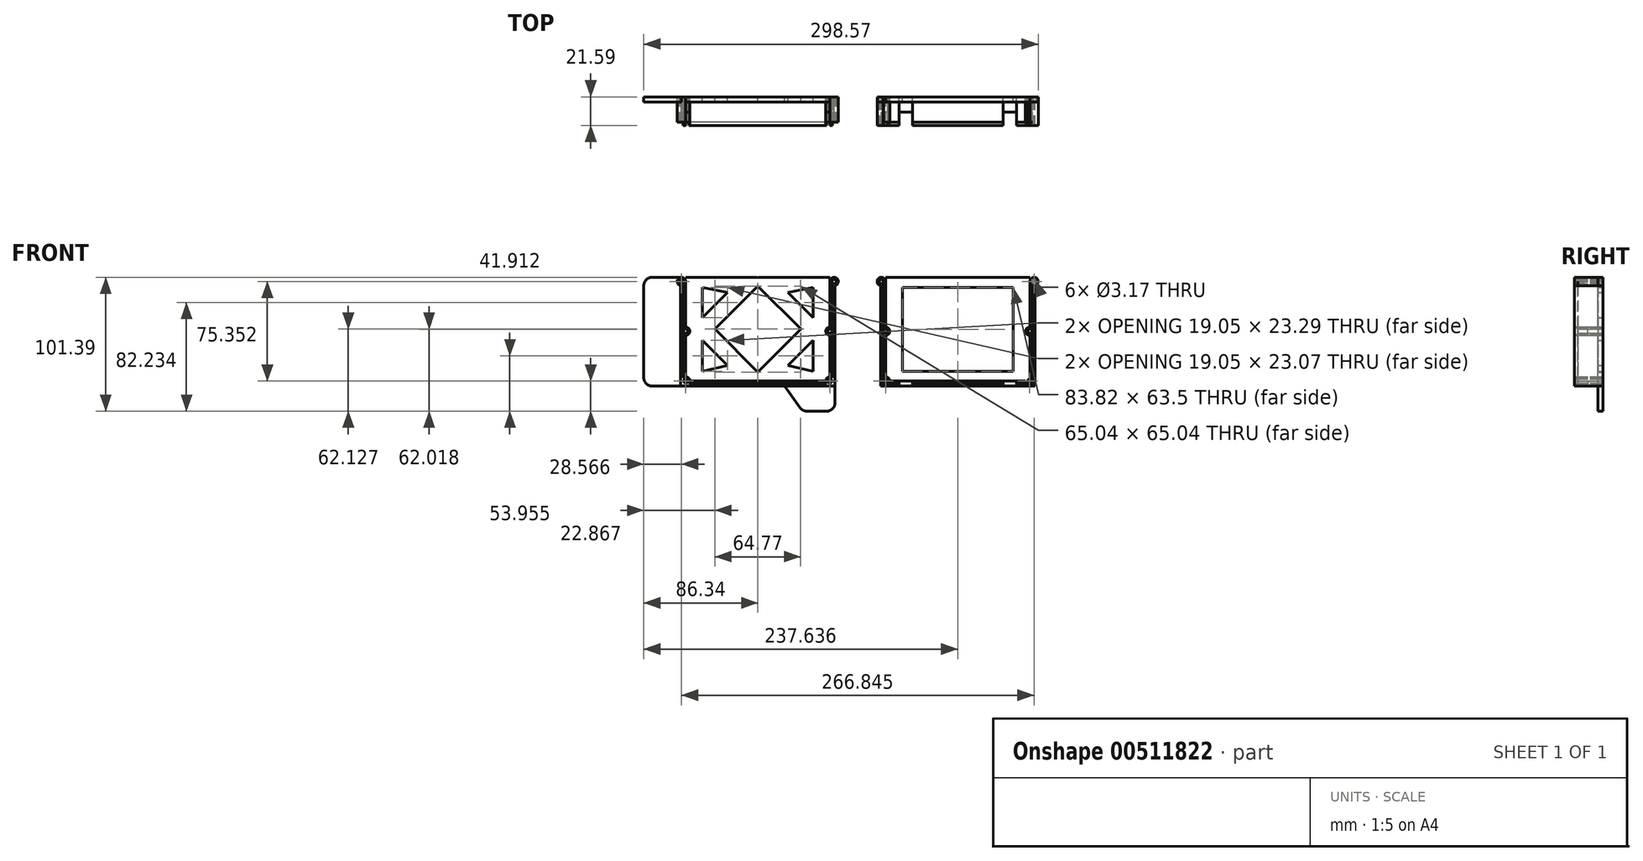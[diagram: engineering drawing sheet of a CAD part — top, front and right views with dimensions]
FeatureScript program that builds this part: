
annotation { "Feature Type Name" : "Feature", "Feature Type Description" : "" }
export const myFeature = defineFeature(function(context is Context, id is Id, definition is map)
    precondition{}
    {
        {
            var Q0;
            Q0=qCreatedBy(makeId("Front.planeOp"),FACE);
            var sketch = newSketch(context, id + "F0", { "sketchPlane" : qUnion([Q0])});
            skLineSegment(sketch, "E0.top", {"start": v(57.8, 40.84) * mm, "end": v(-57.77, 40.84) * mm});
            skPoint(sketch, "E0.middle", {"position": v(0, 0) * mm});
            skLineSegment(sketch, "E1.0", {"start": v(51.44, -37.67) * mm, "end": v(-51.34, -37.67) * mm});
            skLineSegment(sketch, "E2.0", {"start": v(-54.61, -34.5) * mm, "end": v(-54.61, -3.17) * mm});
            skLineSegment(sketch, "E3.0", {"start": v(54.6, -34.5) * mm, "end": v(54.6, -3.17) * mm});
            skLineSegment(sketch, "E4.0", {"start": v(-41.91, -30.27) * mm, "end": v(-41.91, -6.98) * mm});
            skLineSegment(sketch, "E5.0", {"start": v(41.91, -30.27) * mm, "end": v(41.91, -6.98) * mm});
            skLineSegment(sketch, "E6", {"start": v(-41.91, 10.16) * mm, "end": v(-22.86, 29.21) * mm});
            skLineSegment(sketch, "E7", {"start": v(-41.91, -6.98) * mm, "end": v(-22.86, -26.03) * mm});
            skLineSegment(sketch, "E8", {"start": v(22.86, -26.03) * mm, "end": v(41.9, -6.98) * mm});
            skLineSegment(sketch, "E9", {"start": v(41.9, 10.16) * mm, "end": v(22.86, 29.21) * mm});
            skLineSegment(sketch, "E10.trimOffspring", {"start": v(-41.91, 10.16) * mm, "end": v(-41.91, 33.23) * mm});
            skLineSegment(sketch, "E11.trimOffspring", {"start": v(41.91, 10.16) * mm, "end": v(41.91, 33.23) * mm});
            skLineSegment(sketch, "E12.trimOffspring", {"start": v(-22.86, 29.21) * mm, "end": v(-41.91, 33.23) * mm});
            skLineSegment(sketch, "E13.trimOffspring", {"start": v(-22.86, -26.03) * mm, "end": v(-41.91, -30.27) * mm});
            skLineSegment(sketch, "E14.trimOffspring", {"start": v(41.91, 33.23) * mm, "end": v(22.86, 29.21) * mm});
            skLineSegment(sketch, "E15.trimOffspring", {"start": v(41.91, -30.27) * mm, "end": v(22.86, -26.03) * mm});
            skLineSegment(sketch, "E16.0", {"start": v(-32.52, 1.59) * mm, "end": v(0, 34.1) * mm});
            skLineSegment(sketch, "E17.0", {"start": v(32.52, 1.59) * mm, "end": v(0, 34.1) * mm});
            skLineSegment(sketch, "E18.0", {"start": v(0, -30.93) * mm, "end": v(32.52, 1.59) * mm});
            skLineSegment(sketch, "E19.0", {"start": v(-32.52, 1.59) * mm, "end": v(0, -30.93) * mm});
            skArc(sketch, "E20", {"start": v(-54.61, -3.17) * mm, "mid": v(-51.44, 0) * mm, "end": v(-54.61, 3.18) * mm});
            skPoint(sketch, "E20.centerSnap0", {"position": v(-57.79, 0) * mm});
            skPoint(sketch, "E21.centerSnap0", {"position": v(57.79, 0) * mm});
            skArc(sketch, "E22", {"start": v(54.6, -34.5) * mm, "mid": v(52.36, -35.43) * mm, "end": v(51.44, -37.67) * mm});
            skPoint(sketch, "E23.second.point", {"position": v(54.6, 38.74) * mm});
            skPoint(sketch, "E23.third.point", {"position": v(60.92, 37.5) * mm});
            skLineSegment(sketch, "E24.trimOffspring", {"start": v(54.6, 3.18) * mm, "end": v(54.6, 40.84) * mm});
            skPoint(sketch, "E21.center.orphan", {"position": v(54.6, 0) * mm});
            skCircle(sketch, "E25", {"center": v(54.6, 0) * mm, "radius": 3.18 * mm});
            skCircle(sketch, "E26", {"center": v(54.6, 0) * mm, "radius": 1.6 * mm});
            skCircle(sketch, "E27", {"center": v(-54.61, 0) * mm, "radius": 3.18 * mm});
            skCircle(sketch, "E28", {"center": v(-54.61, 0) * mm, "radius": 1.6 * mm});
            skCircle(sketch, "E29", {"center": v(54.6, -37.67) * mm, "radius": 1.59 * mm});
            skCircle(sketch, "E30", {"center": v(54.6, -37.67) * mm, "radius": 3.18 * mm});
            skCircle(sketch, "E31", {"center": v(-54.51, -37.67) * mm, "radius": 3.17 * mm});
            skCircle(sketch, "E32", {"center": v(-54.51, -37.67) * mm, "radius": 1.59 * mm});
            skCircle(sketch, "E33", {"center": v(-57.77, 37.68) * mm, "radius": 3.16 * mm});
            skCircle(sketch, "E34", {"center": v(57.79, 37.67) * mm, "radius": 3.18 * mm});
            skCircle(sketch, "E35", {"center": v(-57.77, 37.68) * mm, "radius": 1.59 * mm});
            skCircle(sketch, "E36", {"center": v(57.79, 37.67) * mm, "radius": 1.6 * mm});
            skLineSegment(sketch, "E37", {"start": v(75.65, 45.82) * mm, "end": v(75.65, -59.82) * mm, "construction": true});
            skCircle(sketch, "E38.MirrorC", {"center": v(93.51, 37.67) * mm, "radius": 1.6 * mm});
            skCircle(sketch, "E39.MirrorC", {"center": v(209.07, 37.68) * mm, "radius": 1.59 * mm});
            skCircle(sketch, "E40.MirrorC", {"center": v(205.8, -37.67) * mm, "radius": 1.59 * mm});
            skCircle(sketch, "E41.MirrorC", {"center": v(96.69, 0) * mm, "radius": 1.6 * mm});
            skCircle(sketch, "E42.MirrorC", {"center": v(205.9, 0) * mm, "radius": 3.18 * mm});
            skCircle(sketch, "E43.MirrorC", {"center": v(96.69, -37.67) * mm, "radius": 1.59 * mm});
            skArc(sketch, "E44.MirrorCS", {"start": v(205.9, -3.17) * mm, "mid": v(202.73, 0) * mm, "end": v(205.9, 3.18) * mm});
            skCircle(sketch, "E45.MirrorC", {"center": v(96.69, 0) * mm, "radius": 3.18 * mm});
            skLineSegment(sketch, "E46.MirrorCS", {"start": v(99.86, -37.67) * mm, "end": v(202.63, -37.67) * mm});
            skCircle(sketch, "E47.MirrorC", {"center": v(205.9, 0) * mm, "radius": 1.6 * mm});
            skLineSegment(sketch, "E48.MirrorCS", {"start": v(205.9, -34.5) * mm, "end": v(205.9, -3.17) * mm});
            skLineSegment(sketch, "E49.MirrorCS", {"start": v(96.69, -34.5) * mm, "end": v(96.69, -3.17) * mm});
            skPoint(sketch, "E50.MirrorP", {"position": v(209.08, 0) * mm});
            skArc(sketch, "E51.MirrorCS", {"start": v(96.69, -34.5) * mm, "mid": v(98.93, -35.43) * mm, "end": v(99.86, -37.67) * mm});
            skCircle(sketch, "E52.MirrorC", {"center": v(209.07, 37.68) * mm, "radius": 3.16 * mm});
            skCircle(sketch, "E53.MirrorC", {"center": v(93.51, 37.67) * mm, "radius": 3.18 * mm});
            skLineSegment(sketch, "E54.MirrorCS", {"start": v(96.69, 3.18) * mm, "end": v(96.69, 40.84) * mm});
            skLineSegment(sketch, "E55.MirrorCS", {"start": v(93.5, 40.84) * mm, "end": v(209.07, 40.84) * mm});
            skPoint(sketch, "E56.MirrorP", {"position": v(90.38, 37.5) * mm});
            skLineSegment(sketch, "E57.MirrorCS", {"start": v(90.38, 37.5) * mm, "end": v(90.38, 37.16) * mm});
            skCircle(sketch, "E58.MirrorC", {"center": v(205.8, -37.67) * mm, "radius": 3.17 * mm});
            skCircle(sketch, "E59.MirrorC", {"center": v(96.69, -37.67) * mm, "radius": 3.18 * mm});
            skPoint(sketch, "E60.MirrorP", {"position": v(151.3, 0) * mm});
            skPoint(sketch, "E61.MirrorP", {"position": v(93.51, 0) * mm});
            skPoint(sketch, "E62.MirrorP", {"position": v(96.69, 38.74) * mm});
            skLineSegment(sketch, "E63.MirrorCS", {"start": v(205.9, 3.18) * mm, "end": v(205.9, 40.85) * mm});
            skLineSegment(sketch, "E64", {"start": v(109.39, 33.23) * mm, "end": v(193.2, 33.23) * mm});
            skLineSegment(sketch, "E65", {"start": v(109.39, 33.23) * mm, "end": v(109.39, -30.27) * mm});
            skLineSegment(sketch, "E66", {"start": v(109.39, -30.27) * mm, "end": v(193.2, -30.27) * mm});
            skLineSegment(sketch, "E67", {"start": v(193.2, 33.23) * mm, "end": v(193.2, -30.27) * mm});
            skLineSegment(sketch, "E68.0", {"start": v(185.59, -41.48) * mm, "end": v(185.59, -37.67) * mm});
            skLineSegment(sketch, "E69", {"start": v(195.75, -37.67) * mm, "end": v(195.75, -41.48) * mm});
            skLineSegment(sketch, "E70", {"start": v(117, -37.67) * mm, "end": v(117, -41.48) * mm});
            skLineSegment(sketch, "E71", {"start": v(106.85, -37.67) * mm, "end": v(106.85, -41.48) * mm});
            skLineSegment(sketch, "E72", {"start": v(-57.77, 40.84) * mm, "end": v(-79.99, 40.84) * mm});
            skPoint(sketch, "E73.visualSharp", {"position": v(-86.34, 40.84) * mm});
            skArc(sketch, "E73.filletArc", {"start": v(-79.99, 40.84) * mm, "mid": v(-84.48, 38.98) * mm, "end": v(-86.34, 34.5) * mm});
            skLineSegment(sketch, "E74.0", {"start": v(-58.4, 34.58) * mm, "end": v(-58.4, -41.49) * mm});
            skLineSegment(sketch, "E75.1", {"start": v(58.43, -41.49) * mm, "end": v(-58.4, -41.49) * mm});
            skLineSegment(sketch, "E76.0", {"start": v(52.07, -39.58) * mm, "end": v(-51.97, -39.58) * mm});
            skLineSegment(sketch, "E77", {"start": v(58.42, -44.02) * mm, "end": v(58.42, -54.19) * mm});
            skLineSegment(sketch, "E78.trimOffspring", {"start": v(56.51, -2.54) * mm, "end": v(56.51, -35.13) * mm});
            skLineSegment(sketch, "E79.trimOffspring", {"start": v(58.38, 34.55) * mm, "end": v(58.42, -44.02) * mm});
            skLineSegment(sketch, "E80.trimOffspring", {"start": v(56.52, 34.76) * mm, "end": v(56.52, 2.54) * mm});
            skLineSegment(sketch, "E81.trimOffspring", {"start": v(-56.52, 34.78) * mm, "end": v(-56.51, 2.54) * mm});
            skLineSegment(sketch, "E82.trimOffspring", {"start": v(-56.51, -2.54) * mm, "end": v(-56.51, -35.21) * mm});
            skLineSegment(sketch, "E83", {"start": v(37.17, -60.54) * mm, "end": v(52.07, -60.54) * mm});
            skLineSegment(sketch, "E84", {"start": v(20.43, -41.49) * mm, "end": v(31.98, -57.85) * mm});
            skLineSegment(sketch, "E85", {"start": v(-79.99, -41.49) * mm, "end": v(-58.4, -41.49) * mm});
            skLineSegment(sketch, "E86", {"start": v(-86.34, 34.5) * mm, "end": v(-86.34, -35.14) * mm});
            skLineSegment(sketch, "E87", {"start": v(-54.61, 3.18) * mm, "end": v(-54.61, 40.84) * mm});
            skLineSegment(sketch, "E88.trimOffspring", {"start": v(94.77, 34.76) * mm, "end": v(94.77, 2.53) * mm});
            skLineSegment(sketch, "E89.trimOffspring", {"start": v(207.8, 34.78) * mm, "end": v(207.8, 2.55) * mm});
            skLineSegment(sketch, "E90.trimOffspring", {"start": v(99.23, -39.57) * mm, "end": v(203.26, -39.57) * mm});
            skLineSegment(sketch, "E91.trimOffspring", {"start": v(207.8, -2.55) * mm, "end": v(207.8, -35.2) * mm});
            skLineSegment(sketch, "E92.trimOffspring", {"start": v(94.77, -2.53) * mm, "end": v(94.77, -35.14) * mm});
            skLineSegment(sketch, "E93.0", {"start": v(92.88, -41.48) * mm, "end": v(209.7, -41.48) * mm});
            skLineSegment(sketch, "E94.0", {"start": v(209.7, 34.58) * mm, "end": v(209.7, -41.48) * mm});
            skLineSegment(sketch, "E95.trimOffspring", {"start": v(92.92, 34.55) * mm, "end": v(92.88, -41.48) * mm});
            skLineSegment(sketch, "E96", {"start": v(94.77, 2.53) * mm, "end": v(94.77, 47.7) * mm});
            skPoint(sketch, "E97.visualSharp", {"position": v(-86.34, -41.49) * mm});
            skArc(sketch, "E97.filletArc", {"start": v(-86.34, -35.14) * mm, "mid": v(-84.48, -39.63) * mm, "end": v(-79.99, -41.49) * mm});
            skPoint(sketch, "E98.visualSharp", {"position": v(33.88, -60.54) * mm});
            skArc(sketch, "E98.filletArc", {"start": v(31.98, -57.85) * mm, "mid": v(34.25, -59.83) * mm, "end": v(37.17, -60.54) * mm});
            skPoint(sketch, "E99.visualSharp", {"position": v(58.42, -60.54) * mm});
            skArc(sketch, "E99.filletArc", {"start": v(52.07, -60.54) * mm, "mid": v(56.56, -58.68) * mm, "end": v(58.42, -54.19) * mm});
            skSolve(sketch);
        }
        {
            var Q0;
            {var subQ18=sQuery(id+"F0.wireOp",EDGE,"E48.MirrorCS");Q0=makeQuery(id+"F0.imprint","IMPRINT",FACE,{"disambiguationData":[TD([[makeQuery(id+"F0.imprint","IMPRINT",EDGE,{"derivedFrom":subQ18}),1.0]])]});}
            var Q1;
            {var subQ0=sQuery(id+"F0.wireOp",EDGE,"E427.MirrorCS");var subQ1=sQuery(id+"F0.wireOp",EDGE,"E38.MirrorC");var subQ2=makeQuery(id+"F0.imprint","INTERSECT",VERTEX,{"disambiguationData":[OD(0.0)],"derivedFrom":[subQ1,subQ0]});Q1=makeQuery(id+"F0.imprint","IMPRINT",FACE,{"disambiguationData":[TD([[makeQuery(id+"F0.imprint","IMPRINT",EDGE,{"disambiguationData":[TD([[subQ2,1.0]])],"derivedFrom":subQ1}),-1.0]])]});}
            var Q2;
            {var subQ0=sQuery(id+"F0.wireOp",EDGE,"E427.MirrorCS");var subQ1=sQuery(id+"F0.wireOp",EDGE,"E38.MirrorC");var subQ2=makeQuery(id+"F0.imprint","INTERSECT",VERTEX,{"disambiguationData":[OD(0.0)],"derivedFrom":[subQ1,subQ0]});Q2=makeQuery(id+"F0.imprint","IMPRINT",FACE,{"disambiguationData":[TD([[makeQuery(id+"F0.imprint","IMPRINT",EDGE,{"disambiguationData":[TD([[subQ2,-1.0]])],"derivedFrom":subQ1}),-1.0]])]});}
            var Q3;
            Q3=makeQuery(id+"F0.imprint","IMPRINT",FACE,{"disambiguationData":[TD([[makeQuery(id+"F0.imprint","IMPRINT",EDGE,{"derivedFrom":sQuery(id+"F0.wireOp",EDGE,"E43.MirrorC")}),-1.0]])]});
            var Q4;
            Q4=makeQuery(id+"F0.imprint","IMPRINT",FACE,{"disambiguationData":[TD([[makeQuery(id+"F0.imprint","IMPRINT",EDGE,{"derivedFrom":sQuery(id+"F0.wireOp",EDGE,"E40.MirrorC")}),-1.0]])]});
            var Q5;
            {var subQ0=sQuery(id+"F0.wireOp",EDGE,"E392.MirrorCS");var subQ1=sQuery(id+"F0.wireOp",EDGE,"E39.MirrorC");var subQ2=makeQuery(id+"F0.imprint","INTERSECT",VERTEX,{"disambiguationData":[OD(0.0)],"derivedFrom":[subQ1,subQ0]});Q5=makeQuery(id+"F0.imprint","IMPRINT",FACE,{"disambiguationData":[TD([[makeQuery(id+"F0.imprint","IMPRINT",EDGE,{"disambiguationData":[TD([[subQ2,1.0]])],"derivedFrom":subQ1}),-1.0]])]});}
            var Q6;
            {var subQ0=sQuery(id+"F0.wireOp",EDGE,"E392.MirrorCS");var subQ1=sQuery(id+"F0.wireOp",EDGE,"E39.MirrorC");var subQ2=makeQuery(id+"F0.imprint","INTERSECT",VERTEX,{"disambiguationData":[OD(0.0)],"derivedFrom":[subQ1,subQ0]});Q6=makeQuery(id+"F0.imprint","IMPRINT",FACE,{"disambiguationData":[TD([[makeQuery(id+"F0.imprint","IMPRINT",EDGE,{"disambiguationData":[TD([[subQ2,-1.0]])],"derivedFrom":subQ1}),-1.0]])]});}
            var Q7;
            Q7=makeQuery(id+"F0.imprint","IMPRINT",FACE,{"disambiguationData":[TD([[makeQuery(id+"F0.imprint","IMPRINT",EDGE,{"derivedFrom":sQuery(id+"F0.wireOp",EDGE,"E39.MirrorC")}),-1.0]])]});
            extrude(context, id + "F1", {"entities" : qUnion([Q0, Q1, Q2, Q3, Q4, Q5, Q6, Q7]), "depth" : 3.8 * mm});
        }
        {
            var Q0;
            Q0=makeQuery(id+"F0.imprint","IMPRINT",FACE,{"disambiguationData":[TD([[makeQuery(id+"F0.imprint","IMPRINT",EDGE,{"derivedFrom":sQuery(id+"F0.wireOp",EDGE,"E41.MirrorC")}),1.0]])]});
            var Q1;
            {var subQ0=sQuery(id+"F0.wireOp",EDGE,"E70");var subQ1=sQuery(id+"F0.wireOp",EDGE,"E46.MirrorCS");var subQ2=makeQuery(id+"F0.imprint","INTERSECT",VERTEX,{"derivedFrom":[subQ1,subQ0]});Q1=makeQuery(id+"F0.imprint","IMPRINT",FACE,{"disambiguationData":[TD([[makeQuery(id+"F0.imprint","IMPRINT",EDGE,{"disambiguationData":[TD([[subQ2,1.0]])],"derivedFrom":subQ1}),-1.0]])]});}
            var Q2;
            {var subQ0=sQuery(id+"F0.wireOp",EDGE,"E71");var subQ1=sQuery(id+"F0.wireOp",EDGE,"E408.MirrorCS");var subQ2=makeQuery(id+"F0.imprint","INTERSECT",VERTEX,{"derivedFrom":[subQ1,subQ0]});Q2=makeQuery(id+"F0.imprint","IMPRINT",FACE,{"disambiguationData":[TD([[makeQuery(id+"F0.imprint","IMPRINT",EDGE,{"disambiguationData":[TD([[subQ2,-1.0]])],"derivedFrom":subQ1}),-1.0]])]});}
            var Q3;
            {var subQ0=sQuery(id+"F0.wireOp",EDGE,"E68.0");var subQ1=sQuery(id+"F0.wireOp",EDGE,"E46.MirrorCS");var subQ2=makeQuery(id+"F0.imprint","INTERSECT",VERTEX,{"derivedFrom":[subQ1,subQ0]});Q3=makeQuery(id+"F0.imprint","IMPRINT",FACE,{"disambiguationData":[TD([[makeQuery(id+"F0.imprint","IMPRINT",EDGE,{"disambiguationData":[TD([[subQ2,-1.0]])],"derivedFrom":subQ1}),-1.0]])]});}
            var Q4;
            {var subQ0=sQuery(id+"F0.wireOp",EDGE,"E68.0");var subQ1=sQuery(id+"F0.wireOp",EDGE,"E408.MirrorCS");var subQ2=makeQuery(id+"F0.imprint","INTERSECT",VERTEX,{"derivedFrom":[subQ1,subQ0]});Q4=makeQuery(id+"F0.imprint","IMPRINT",FACE,{"disambiguationData":[TD([[makeQuery(id+"F0.imprint","IMPRINT",EDGE,{"disambiguationData":[TD([[subQ2,-1.0]])],"derivedFrom":subQ1}),-1.0]])]});}
            var Q5;
            Q5=makeQuery(id+"F0.imprint","IMPRINT",FACE,{"disambiguationData":[TD([[makeQuery(id+"F0.imprint","IMPRINT",EDGE,{"derivedFrom":sQuery(id+"F0.wireOp",EDGE,"E47.MirrorC")}),1.0]])]});
            var Q6;
            {var subQ0=sQuery(id+"F0.wireOp",EDGE,"E93.0");var subQ1=sQuery(id+"F0.wireOp",EDGE,"E70");var subQ2=makeQuery(id+"F0.imprint","INTERSECT",VERTEX,{"derivedFrom":[subQ1,subQ0]});Q6=makeQuery(id+"F0.imprint","IMPRINT",FACE,{"disambiguationData":[TD([[makeQuery(id+"F0.imprint","IMPRINT",EDGE,{"disambiguationData":[TD([[subQ2,1.0]])],"derivedFrom":subQ1}),-1.0]])]});}
            var Q7;
            {var subQ0=sQuery(id+"F0.wireOp",EDGE,"E93.0");var subQ1=sQuery(id+"F0.wireOp",EDGE,"E68.0");var subQ2=makeQuery(id+"F0.imprint","INTERSECT",VERTEX,{"derivedFrom":[subQ1,subQ0]});Q7=makeQuery(id+"F0.imprint","IMPRINT",FACE,{"disambiguationData":[TD([[makeQuery(id+"F0.imprint","IMPRINT",EDGE,{"disambiguationData":[TD([[subQ2,-1.0]])],"derivedFrom":subQ1}),-1.0]])]});}
            extrude(context, id + "F2", {"entities" : qUnion([Q0, Q1, Q2, Q3, Q4, Q5, Q6, Q7]), "operationType" : NewBodyOperationType.ADD, "depth" : 11.43 * mm});
        }
        {
            var Q0;
            {var subQ0=sQuery(id+"F0.wireOp",EDGE,"E54.MirrorCS");var subQ1=sQuery(id+"F0.wireOp",EDGE,"E45.MirrorC");var subQ2=makeQuery(id+"F0.imprint","INTERSECT",VERTEX,{"derivedFrom":[subQ1,subQ0]});Q0=makeQuery(id+"F0.imprint","IMPRINT",FACE,{"disambiguationData":[TD([[makeQuery(id+"F0.imprint","IMPRINT",EDGE,{"disambiguationData":[TD([[subQ2,1.0]])],"derivedFrom":subQ1}),1.0]])]});}
            var Q1;
            {var subQ3=sQuery(id+"F0.wireOp",EDGE,"E92.trimOffspring");Q1=makeQuery(id+"F0.imprint","IMPRINT",FACE,{"disambiguationData":[TD([[makeQuery(id+"F0.imprint","IMPRINT",EDGE,{"derivedFrom":subQ3}),1.0]])]});}
            var Q2;
            {var subQ0=sQuery(id+"F0.wireOp",EDGE,"E71");var subQ1=sQuery(id+"F0.wireOp",EDGE,"E46.MirrorCS");var subQ2=makeQuery(id+"F0.imprint","INTERSECT",VERTEX,{"derivedFrom":[subQ1,subQ0]});Q2=makeQuery(id+"F0.imprint","IMPRINT",FACE,{"disambiguationData":[TD([[makeQuery(id+"F0.imprint","IMPRINT",EDGE,{"disambiguationData":[TD([[subQ2,1.0]])],"derivedFrom":subQ1}),-1.0]])]});}
            var Q3;
            {var subQ0=sQuery(id+"F0.wireOp",EDGE,"E68.0");var subQ1=sQuery(id+"F0.wireOp",EDGE,"E46.MirrorCS");var subQ2=makeQuery(id+"F0.imprint","INTERSECT",VERTEX,{"derivedFrom":[subQ1,subQ0]});Q3=makeQuery(id+"F0.imprint","IMPRINT",FACE,{"disambiguationData":[TD([[makeQuery(id+"F0.imprint","IMPRINT",EDGE,{"disambiguationData":[TD([[subQ2,1.0]])],"derivedFrom":subQ1}),-1.0]])]});}
            var Q4;
            {var subQ0=sQuery(id+"F0.wireOp",EDGE,"E58.MirrorC");var subQ1=sQuery(id+"F0.wireOp",EDGE,"E46.MirrorCS");var subQ2=makeQuery(id+"F0.imprint","INTERSECT",VERTEX,{"derivedFrom":[subQ1,subQ0]});Q4=makeQuery(id+"F0.imprint","IMPRINT",FACE,{"disambiguationData":[TD([[makeQuery(id+"F0.imprint","IMPRINT",EDGE,{"disambiguationData":[TD([[subQ2,1.0]])],"derivedFrom":subQ1}),-1.0]])]});}
            var Q5;
            {var subQ0=sQuery(id+"F0.wireOp",EDGE,"E48.MirrorCS");Q5=makeQuery(id+"F0.imprint","IMPRINT",FACE,{"disambiguationData":[TD([[makeQuery(id+"F0.imprint","IMPRINT",EDGE,{"derivedFrom":subQ0}),-1.0]])]});}
            var Q6;
            {var subQ3=sQuery(id+"F0.wireOp",EDGE,"E89.trimOffspring");Q6=makeQuery(id+"F0.imprint","IMPRINT",FACE,{"disambiguationData":[TD([[makeQuery(id+"F0.imprint","IMPRINT",EDGE,{"derivedFrom":subQ3}),-1.0]])]});}
            extrude(context, id + "F3", {"entities" : qUnion([Q0, Q1, Q2, Q3, Q4, Q5, Q6]), "depth" : 19.05 * mm});
        }
        {
            var Q0;
            {var subQ7=sQuery(id+"F0.wireOp",EDGE,"E92.trimOffspring");Q0=makeQuery(id+"F0.imprint","IMPRINT",FACE,{"disambiguationData":[TD([[makeQuery(id+"F0.imprint","IMPRINT",EDGE,{"derivedFrom":subQ7}),-1.0]])]});}
            var Q1;
            {var subQ0=sQuery(id+"F0.wireOp",EDGE,"E93.0");var subQ1=sQuery(id+"F0.wireOp",EDGE,"E68.0");var subQ2=makeQuery(id+"F0.imprint","INTERSECT",VERTEX,{"derivedFrom":[subQ1,subQ0]});Q1=makeQuery(id+"F0.imprint","IMPRINT",FACE,{"disambiguationData":[TD([[makeQuery(id+"F0.imprint","IMPRINT",EDGE,{"disambiguationData":[TD([[subQ2,-1.0]])],"derivedFrom":subQ1}),1.0]])]});}
            var Q2;
            {var subQ8=sQuery(id+"F0.wireOp",EDGE,"E89.trimOffspring");Q2=makeQuery(id+"F0.imprint","IMPRINT",FACE,{"disambiguationData":[TD([[makeQuery(id+"F0.imprint","IMPRINT",EDGE,{"derivedFrom":subQ8}),1.0]])]});}
            var Q3;
            Q3=makeQuery(id+"F0.imprint","IMPRINT",FACE,{"disambiguationData":[TD([[makeQuery(id+"F0.imprint","IMPRINT",EDGE,{"derivedFrom":sQuery(id+"F0.wireOp",EDGE,"E40.MirrorC")}),1.0]])]});
            var Q4;
            Q4=makeQuery(id+"F0.imprint","IMPRINT",FACE,{"disambiguationData":[TD([[makeQuery(id+"F0.imprint","IMPRINT",EDGE,{"derivedFrom":sQuery(id+"F0.wireOp",EDGE,"E39.MirrorC")}),1.0]])]});
            var Q5;
            {var subQ0=sQuery(id+"F0.wireOp",EDGE,"E96");var subQ7=sQuery(id+"F0.wireOp",EDGE,"E38.MirrorC");var subQ8=makeQuery(id+"F0.imprint","INTERSECT",VERTEX,{"disambiguationData":[OD(0.0)],"derivedFrom":[subQ7,subQ0]});Q5=makeQuery(id+"F0.imprint","IMPRINT",FACE,{"disambiguationData":[TD([[makeQuery(id+"F0.imprint","IMPRINT",EDGE,{"disambiguationData":[TD([[subQ8,1.0]])],"derivedFrom":subQ7}),1.0]])]});}
            var Q6;
            {var subQ0=sQuery(id+"F0.wireOp",EDGE,"E96");var subQ1=sQuery(id+"F0.wireOp",EDGE,"E53.MirrorC");var subQ2=makeQuery(id+"F0.imprint","INTERSECT",VERTEX,{"disambiguationData":[OD(0.0)],"derivedFrom":[subQ1,subQ0]});Q6=makeQuery(id+"F0.imprint","IMPRINT",FACE,{"disambiguationData":[TD([[makeQuery(id+"F0.imprint","IMPRINT",EDGE,{"disambiguationData":[TD([[subQ2,-1.0]])],"derivedFrom":subQ1}),1.0]])]});}
            var Q7;
            {var subQ0=sQuery(id+"F0.wireOp",EDGE,"E53.MirrorC");var subQ1=makeQuery(id+"F0.imprint","IMPRINT",VERTEX,{"derivedFrom":subQ0});Q7=makeQuery(id+"F0.imprint","IMPRINT",FACE,{"disambiguationData":[TD([[makeQuery(id+"F0.imprint","IMPRINT",EDGE,{"disambiguationData":[TD([[subQ1,1.0]])],"derivedFrom":subQ0}),-1.0]])]});}
            var Q8;
            {var subQ0=sQuery(id+"F0.wireOp",EDGE,"E55.MirrorCS");var subQ1=sQuery(id+"F0.wireOp",EDGE,"E52.MirrorC");var subQ2=makeQuery(id+"F0.imprint","INTERSECT",VERTEX,{"derivedFrom":[subQ1,subQ0]});Q8=makeQuery(id+"F0.imprint","IMPRINT",FACE,{"disambiguationData":[TD([[makeQuery(id+"F0.imprint","IMPRINT",EDGE,{"disambiguationData":[TD([[subQ2,1.0]])],"derivedFrom":subQ1}),1.0]])]});}
            var Q9;
            Q9=makeQuery(id+"F0.imprint","IMPRINT",FACE,{"disambiguationData":[TD([[makeQuery(id+"F0.imprint","IMPRINT",EDGE,{"derivedFrom":sQuery(id+"F0.wireOp",EDGE,"E43.MirrorC")}),1.0]])]});
            extrude(context, id + "F4", {"entities" : qUnion([Q0, Q1, Q2, Q3, Q4, Q5, Q6, Q7, Q8, Q9]), "oppositeDirection" : true, "depth" : -21.59 * mm});
        }
        {
            var Q0;
            {var subQ10=sQuery(id+"F0.wireOp",EDGE,"E2.0");Q0=makeQuery(id+"F0.imprint","IMPRINT",FACE,{"disambiguationData":[TD([[makeQuery(id+"F0.imprint","IMPRINT",EDGE,{"derivedFrom":subQ10}),-1.0]])]});}
            var Q1;
            {var subQ1=sQuery(id+"F0.wireOp",EDGE,"RHEU3sj8-1iCZ-CM9B-113w-WOaot5dIcocV");Q1=makeQuery(id+"F0.imprint","IMPRINT",FACE,{"disambiguationData":[TD([[makeQuery(id+"F0.imprint","IMPRINT",EDGE,{"derivedFrom":subQ1}),-1.0]])]});}
            var Q2;
            Q2=makeQuery(id+"F0.imprint","IMPRINT",FACE,{"disambiguationData":[TD([[makeQuery(id+"F0.imprint","IMPRINT",EDGE,{"derivedFrom":sQuery(id+"F0.wireOp",EDGE,"3c5441e0-d35e-4564-bf46-5cc15d00bd89.0")}),-1.0]])]});
            var Q3;
            {var subQ3=sQuery(id+"F0.wireOp",EDGE,"c3c61c70-07da-46f8-98a4-32d5f6c03bcd.trimOffspring");Q3=makeQuery(id+"F0.imprint","IMPRINT",FACE,{"disambiguationData":[TD([[makeQuery(id+"F0.imprint","IMPRINT",EDGE,{"derivedFrom":subQ3}),1.0]])]});}
            var Q4;
            {var subQ3=sQuery(id+"F0.wireOp",EDGE,"E77");Q4=makeQuery(id+"F0.imprint","IMPRINT",FACE,{"disambiguationData":[TD([[makeQuery(id+"F0.imprint","IMPRINT",EDGE,{"derivedFrom":subQ3}),-1.0]])]});}
            var Q5;
            {var subQ1=sQuery(id+"F0.wireOp",EDGE,"E72");Q5=makeQuery(id+"F0.imprint","IMPRINT",FACE,{"disambiguationData":[TD([[makeQuery(id+"F0.imprint","IMPRINT",EDGE,{"derivedFrom":subQ1}),1.0]])]});}
            extrude(context, id + "F5", {"entities" : qUnion([Q0, Q1, Q2, Q3, Q4, Q5]), "depth" : 3.8 * mm});
        }
        {
            var Q0;
            Q0=makeQuery(id+"F0.imprint","IMPRINT",FACE,{"disambiguationData":[TD([[makeQuery(id+"F0.imprint","IMPRINT",EDGE,{"derivedFrom":sQuery(id+"F0.wireOp",EDGE,"E28")}),-1.0]])]});
            var Q1;
            Q1=makeQuery(id+"F0.imprint","IMPRINT",FACE,{"disambiguationData":[TD([[makeQuery(id+"F0.imprint","IMPRINT",EDGE,{"derivedFrom":sQuery(id+"F0.wireOp",EDGE,"E26")}),-1.0]])]});
            extrude(context, id + "F6", {"entities" : qUnion([Q0, Q1]), "depth" : 11.43 * mm});
        }
        {
            var Q0;
            {var subQ0=sQuery(id+"F0.wireOp",EDGE,"E2.0");Q0=makeQuery(id+"F0.imprint","IMPRINT",FACE,{"disambiguationData":[TD([[makeQuery(id+"F0.imprint","IMPRINT",EDGE,{"derivedFrom":subQ0}),1.0]])]});}
            var Q1;
            {var subQ5=sQuery(id+"F0.wireOp",EDGE,"E76.0");Q1=makeQuery(id+"F0.imprint","IMPRINT",FACE,{"disambiguationData":[TD([[makeQuery(id+"F0.imprint","IMPRINT",EDGE,{"derivedFrom":subQ5}),-1.0]])]});}
            var Q2;
            {var subQ5=sQuery(id+"F0.wireOp",EDGE,"E78.trimOffspring");Q2=makeQuery(id+"F0.imprint","IMPRINT",FACE,{"disambiguationData":[TD([[makeQuery(id+"F0.imprint","IMPRINT",EDGE,{"derivedFrom":subQ5}),-1.0]])]});}
            var Q3;
            {var subQ5=sQuery(id+"F0.wireOp",EDGE,"E80.trimOffspring");Q3=makeQuery(id+"F0.imprint","IMPRINT",FACE,{"disambiguationData":[TD([[makeQuery(id+"F0.imprint","IMPRINT",EDGE,{"derivedFrom":subQ5}),-1.0]])]});}
            var Q4;
            {var subQ0=sQuery(id+"F0.wireOp",EDGE,"E81.trimOffspring");Q4=makeQuery(id+"F0.imprint","IMPRINT",FACE,{"disambiguationData":[TD([[makeQuery(id+"F0.imprint","IMPRINT",EDGE,{"derivedFrom":subQ0}),1.0]])]});}
            extrude(context, id + "F7", {"entities" : qUnion([Q0, Q1, Q2, Q3, Q4]), "depth" : 21.59 * mm});
        }
        {
            var Q0;
            {var subQ5=sQuery(id+"F0.wireOp",EDGE,"E74.0");Q0=makeQuery(id+"F0.imprint","IMPRINT",FACE,{"disambiguationData":[TD([[makeQuery(id+"F0.imprint","IMPRINT",EDGE,{"derivedFrom":subQ5}),1.0]])]});}
            var Q1;
            Q1=makeQuery(id+"F0.imprint","IMPRINT",FACE,{"disambiguationData":[TD([[makeQuery(id+"F0.imprint","IMPRINT",EDGE,{"derivedFrom":sQuery(id+"F0.wireOp",EDGE,"E36")}),-1.0]])]});
            var Q2;
            {var subQ0=sQuery(id+"F0.wireOp",EDGE,"E22");Q2=makeQuery(id+"F0.imprint","IMPRINT",FACE,{"disambiguationData":[TD([[makeQuery(id+"F0.imprint","IMPRINT",EDGE,{"derivedFrom":subQ0}),1.0]])]});}
            var Q3;
            Q3=makeQuery(id+"F0.imprint","IMPRINT",FACE,{"disambiguationData":[TD([[makeQuery(id+"F0.imprint","IMPRINT",EDGE,{"derivedFrom":sQuery(id+"F0.wireOp",EDGE,"E32")}),-1.0]])]});
            var Q4;
            Q4=makeQuery(id+"F0.imprint","IMPRINT",FACE,{"disambiguationData":[TD([[makeQuery(id+"F0.imprint","IMPRINT",EDGE,{"derivedFrom":sQuery(id+"F0.wireOp",EDGE,"E35")}),-1.0]])]});
            extrude(context, id + "F8", {"entities" : qUnion([Q0, Q1, Q2, Q3, Q4]), "depth" : 19.05 * mm});
        }
    });
